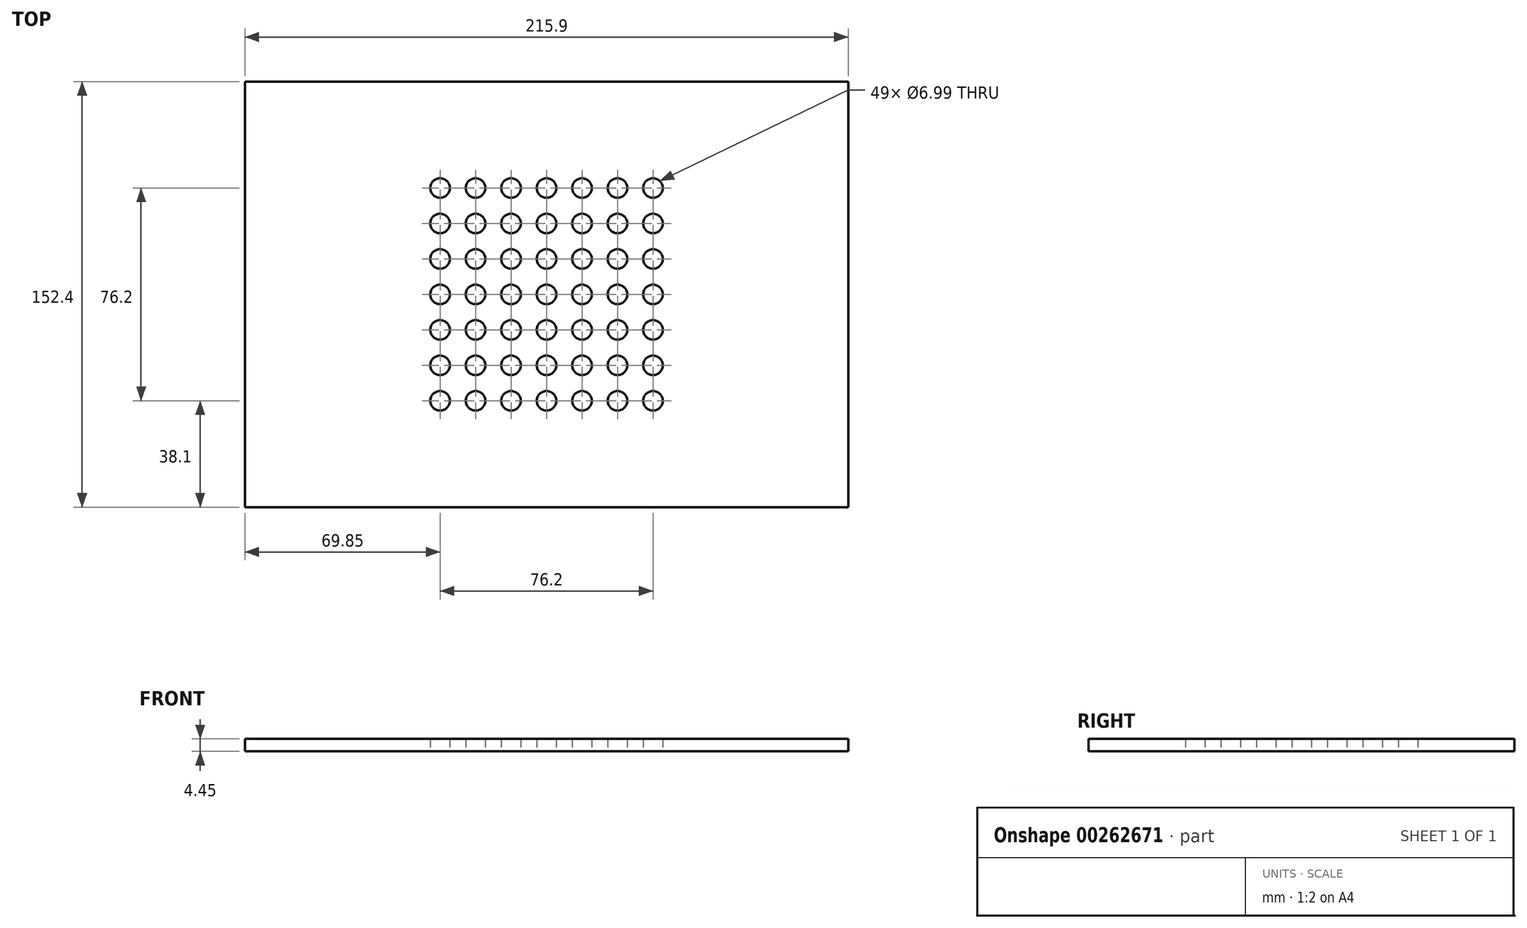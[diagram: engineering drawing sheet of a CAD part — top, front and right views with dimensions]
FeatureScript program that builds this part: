
annotation { "Feature Type Name" : "Feature", "Feature Type Description" : "" }
export const myFeature = defineFeature(function(context is Context, id is Id, definition is map)
    precondition{}
    {
        {
            var Q0;
            Q0=qCreatedBy(makeId("Top.planeOp"),FACE);
            var sketch = newSketch(context, id + "F0", { "sketchPlane" : qUnion([Q0])});
            skLineSegment(sketch, "E0.bottom", {"start": v(0, 0) * mm, "end": v(215.9, 0) * mm});
            skLineSegment(sketch, "E0.top", {"start": v(0, 152.4) * mm, "end": v(215.9, 152.4) * mm});
            skLineSegment(sketch, "E0.left", {"start": v(0, 0) * mm, "end": v(0, 152.4) * mm});
            skLineSegment(sketch, "E0.right", {"start": v(215.9, 0) * mm, "end": v(215.9, 152.4) * mm});
            skCircle(sketch, "E1", {"center": v(107.95, 76.2) * mm, "radius": 3.5 * mm});
            skPoint(sketch, "E1.centerSnap0", {"position": v(107.95, 0) * mm});
            skPoint(sketch, "E1.centerSnap1", {"position": v(0, 76.2) * mm});
            skCircle(sketch, "E2.0.1.0", {"center": v(107.95, 88.9) * mm, "radius": 3.5 * mm});
            skCircle(sketch, "E2.0.2.0", {"center": v(107.95, 101.6) * mm, "radius": 3.5 * mm});
            skCircle(sketch, "E2.0.3.0", {"center": v(107.95, 114.3) * mm, "radius": 3.5 * mm});
            skCircle(sketch, "E2.1.0.0", {"center": v(120.65, 76.2) * mm, "radius": 3.5 * mm});
            skCircle(sketch, "E2.1.1.0", {"center": v(120.65, 88.9) * mm, "radius": 3.5 * mm});
            skCircle(sketch, "E2.1.2.0", {"center": v(120.65, 101.6) * mm, "radius": 3.5 * mm});
            skCircle(sketch, "E2.1.3.0", {"center": v(120.65, 114.3) * mm, "radius": 3.5 * mm});
            skCircle(sketch, "E2.2.0.0", {"center": v(133.35, 76.2) * mm, "radius": 3.5 * mm});
            skCircle(sketch, "E2.2.1.0", {"center": v(133.35, 88.9) * mm, "radius": 3.5 * mm});
            skCircle(sketch, "E2.2.2.0", {"center": v(133.35, 101.6) * mm, "radius": 3.5 * mm});
            skCircle(sketch, "E2.2.3.0", {"center": v(133.35, 114.3) * mm, "radius": 3.5 * mm});
            skCircle(sketch, "E2.3.0.0", {"center": v(146.05, 76.2) * mm, "radius": 3.5 * mm});
            skCircle(sketch, "E2.3.1.0", {"center": v(146.05, 88.9) * mm, "radius": 3.5 * mm});
            skCircle(sketch, "E2.3.2.0", {"center": v(146.05, 101.6) * mm, "radius": 3.5 * mm});
            skCircle(sketch, "E2.3.3.0", {"center": v(146.05, 114.3) * mm, "radius": 3.5 * mm});
            skLineSegment(sketch, "E2.direction1", {"start": v(107.95, 76.2) * mm, "end": v(120.65, 76.2) * mm, "construction": true});
            skLineSegment(sketch, "E2.direction2", {"start": v(107.95, 76.2) * mm, "end": v(107.95, 88.9) * mm, "construction": true});
            skCircle(sketch, "E3.1.1", {"center": v(69.85, 88.9) * mm, "radius": 3.5 * mm});
            skCircle(sketch, "E3.1.2", {"center": v(82.55, 114.3) * mm, "radius": 3.5 * mm});
            skCircle(sketch, "E3.1.3", {"center": v(82.55, 88.9) * mm, "radius": 3.5 * mm});
            skCircle(sketch, "E3.1.5", {"center": v(95.25, 88.9) * mm, "radius": 3.5 * mm});
            skCircle(sketch, "E3.1.8", {"center": v(69.85, 76.2) * mm, "radius": 3.5 * mm});
            skCircle(sketch, "E3.1.9", {"center": v(82.55, 76.2) * mm, "radius": 3.5 * mm});
            skCircle(sketch, "E3.1.10", {"center": v(95.25, 101.6) * mm, "radius": 3.5 * mm});
            skCircle(sketch, "E3.1.11", {"center": v(95.25, 114.3) * mm, "radius": 3.5 * mm});
            skLineSegment(sketch, "E3.1.12", {"start": v(107.95, 76.2) * mm, "end": v(95.25, 76.2) * mm, "construction": true});
            skCircle(sketch, "E3.1.13", {"center": v(69.85, 114.3) * mm, "radius": 3.5 * mm});
            skCircle(sketch, "E3.1.14", {"center": v(82.55, 101.6) * mm, "radius": 3.5 * mm});
            skCircle(sketch, "E3.1.15", {"center": v(69.85, 101.6) * mm, "radius": 3.5 * mm});
            skCircle(sketch, "E3.1.17", {"center": v(95.25, 76.2) * mm, "radius": 3.5 * mm});
            skCircle(sketch, "E3.2.0", {"center": v(82.55, 76.2) * mm, "radius": 3.5 * mm});
            skCircle(sketch, "E3.2.1", {"center": v(95.25, 38.1) * mm, "radius": 3.5 * mm});
            skCircle(sketch, "E3.2.2", {"center": v(69.85, 50.8) * mm, "radius": 3.5 * mm});
            skCircle(sketch, "E3.2.3", {"center": v(95.25, 50.8) * mm, "radius": 3.5 * mm});
            skLineSegment(sketch, "E3.2.4", {"start": v(107.95, 76.2) * mm, "end": v(95.25, 76.2) * mm, "construction": true});
            skCircle(sketch, "E3.2.5", {"center": v(95.25, 63.5) * mm, "radius": 3.5 * mm});
            skCircle(sketch, "E3.2.6", {"center": v(69.85, 76.2) * mm, "radius": 3.5 * mm});
            skCircle(sketch, "E3.2.7", {"center": v(95.25, 76.2) * mm, "radius": 3.5 * mm});
            skCircle(sketch, "E3.2.8", {"center": v(107.95, 38.1) * mm, "radius": 3.5 * mm});
            skCircle(sketch, "E3.2.9", {"center": v(107.95, 50.8) * mm, "radius": 3.5 * mm});
            skCircle(sketch, "E3.2.10", {"center": v(82.55, 63.5) * mm, "radius": 3.5 * mm});
            skCircle(sketch, "E3.2.11", {"center": v(69.85, 63.5) * mm, "radius": 3.5 * mm});
            skLineSegment(sketch, "E3.2.12", {"start": v(107.95, 76.2) * mm, "end": v(107.95, 63.5) * mm, "construction": true});
            skCircle(sketch, "E3.2.13", {"center": v(69.85, 38.1) * mm, "radius": 3.5 * mm});
            skCircle(sketch, "E3.2.14", {"center": v(82.55, 50.8) * mm, "radius": 3.5 * mm});
            skCircle(sketch, "E3.2.15", {"center": v(82.55, 38.1) * mm, "radius": 3.5 * mm});
            skCircle(sketch, "E3.2.17", {"center": v(107.95, 63.5) * mm, "radius": 3.5 * mm});
            skCircle(sketch, "E3.3.0", {"center": v(107.95, 50.8) * mm, "radius": 3.5 * mm});
            skCircle(sketch, "E3.3.1", {"center": v(146.05, 63.5) * mm, "radius": 3.5 * mm});
            skCircle(sketch, "E3.3.2", {"center": v(133.35, 38.1) * mm, "radius": 3.5 * mm});
            skCircle(sketch, "E3.3.3", {"center": v(133.35, 63.5) * mm, "radius": 3.5 * mm});
            skLineSegment(sketch, "E3.3.4", {"start": v(107.95, 76.2) * mm, "end": v(107.95, 63.5) * mm, "construction": true});
            skCircle(sketch, "E3.3.5", {"center": v(120.65, 63.5) * mm, "radius": 3.5 * mm});
            skCircle(sketch, "E3.3.6", {"center": v(107.95, 38.1) * mm, "radius": 3.5 * mm});
            skCircle(sketch, "E3.3.7", {"center": v(107.95, 63.5) * mm, "radius": 3.5 * mm});
            skCircle(sketch, "E3.3.10", {"center": v(120.65, 50.8) * mm, "radius": 3.5 * mm});
            skCircle(sketch, "E3.3.11", {"center": v(120.65, 38.1) * mm, "radius": 3.5 * mm});
            skCircle(sketch, "E3.3.13", {"center": v(146.05, 38.1) * mm, "radius": 3.5 * mm});
            skCircle(sketch, "E3.3.14", {"center": v(133.35, 50.8) * mm, "radius": 3.5 * mm});
            skCircle(sketch, "E3.3.15", {"center": v(146.05, 50.8) * mm, "radius": 3.5 * mm});
            skSolve(sketch);
        }
        {
            var Q0;
            Q0=makeQuery(id+"F0.imprint","IMPRINT",FACE,{"disambiguationData":[TD([[makeQuery(id+"F0.imprint","IMPRINT",EDGE,{"derivedFrom":sQuery(id+"F0.wireOp",EDGE,"E0.bottom")}),1.0]])]});
            extrude(context, id + "F1", {"entities" : qUnion([Q0]), "depth" : 4.44 * mm});
        }
    });
